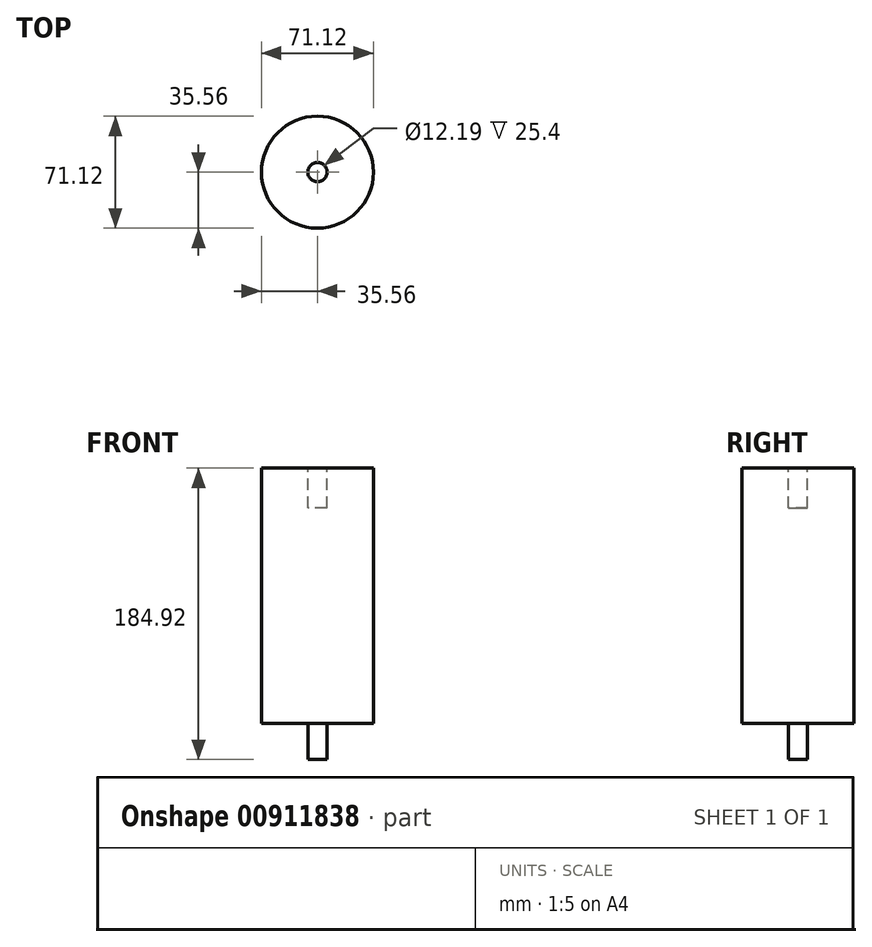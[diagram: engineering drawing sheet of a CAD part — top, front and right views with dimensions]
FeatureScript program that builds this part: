
annotation { "Feature Type Name" : "Feature", "Feature Type Description" : "" }
export const myFeature = defineFeature(function(context is Context, id is Id, definition is map)
    precondition{}
    {
        {
            var Q0;
            Q0=qCreatedBy(makeId("Front.planeOp"),FACE);
            var sketch = newSketch(context, id + "F0", { "sketchPlane" : qUnion([Q0])});
            skLineSegment(sketch, "E0.bottom", {"start": v(0, 86.7) * mm, "end": v(-35.56, 86.7) * mm});
            skLineSegment(sketch, "E0.top", {"start": v(0, -75.36) * mm, "end": v(-35.56, -75.36) * mm});
            skLineSegment(sketch, "E0.left", {"start": v(0, 86.7) * mm, "end": v(0, -75.36) * mm});
            skLineSegment(sketch, "E0.right", {"start": v(-35.56, 86.7) * mm, "end": v(-35.56, -75.36) * mm});
            skLineSegment(sketch, "E1", {"start": v(0, 93.26) * mm, "end": v(0, -84.78) * mm});
            skSolve(sketch);
        }
        {
            var Q0;
            Q0 = qSketchRegion(id + "F0", true);
            var Q1;
            Q1=sQuery(id+"F0.wireOp",EDGE,"E1");
            revolve(context, id + "F1", {"surfaceOperationType" : NewSurfaceOperationType.NEW, "entities" : qUnion([Q0]), "axis" : qUnion([Q1]), "revolveType" : RevolveType.FULL});
        }
        {
            var Q0;
            Q0=makeQuery(id+"F1.opRevolve","SWEPT_FACE",FACE,{"disambiguationData":[OSD([sQuery(id+"F0.wireOp",EDGE,"E0.top")])]});
            var sketch = newSketch(context, id + "F2", { "sketchPlane" : qUnion([Q0])});
            skCircle(sketch, "E2", {"center": v(0, 0) * mm, "radius": 5.97 * mm});
            skSolve(sketch);
        }
        {
            var Q0;
            Q0 = qSketchRegion(id + "F2", true);
            extrude(context, id + "F3", {"entities" : qUnion([Q0]), "operationType" : NewBodyOperationType.ADD, "depth" : 22.86 * mm, "offsetDistance" : 25.4 * mm});
        }
        {
            var Q0;
            Q0=makeQuery(id+"F1.opRevolve","SWEPT_FACE",FACE,{"disambiguationData":[OSD([sQuery(id+"F0.wireOp",EDGE,"E0.bottom")])]});
            var sketch = newSketch(context, id + "F4", { "sketchPlane" : qUnion([Q0])});
            skCircle(sketch, "E3", {"center": v(0, 0) * mm, "radius": 6.1 * mm});
            skSolve(sketch);
        }
        {
            var Q0;
            Q0=makeQuery(id+"F4.imprint","IMPRINT",FACE,{"disambiguationData":[TD([[makeQuery(id+"F4.imprint","IMPRINT",EDGE,{"derivedFrom":sQuery(id+"F4.wireOp",EDGE,"E3")}),1.0]])]});
            extrude(context, id + "F5", {"entities" : qUnion([Q0]), "operationType" : NewBodyOperationType.REMOVE, "oppositeDirection" : true, "depth" : 25.4 * mm, "offsetDistance" : 25.4 * mm});
        }
    });
